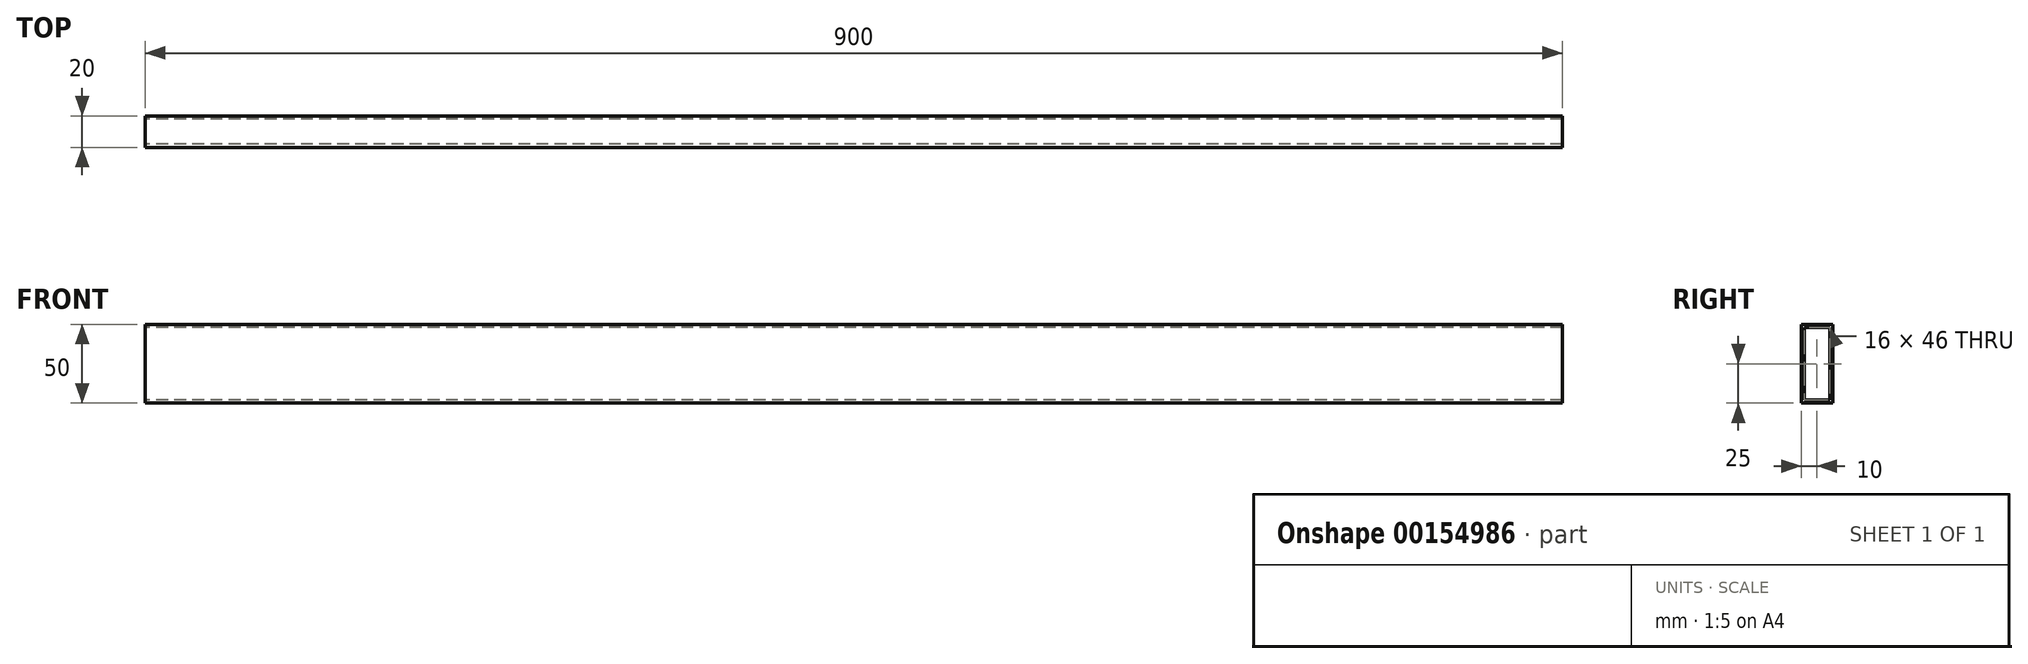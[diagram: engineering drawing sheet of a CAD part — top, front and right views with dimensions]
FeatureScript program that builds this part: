
annotation { "Feature Type Name" : "Feature", "Feature Type Description" : "" }
export const myFeature = defineFeature(function(context is Context, id is Id, definition is map)
    precondition{}
    {
        {
            var Q0;
            Q0=qCreatedBy(makeId("Right.planeOp"),FACE);
            var sketch = newSketch(context, id + "F0", { "sketchPlane" : qUnion([Q0])});
            skLineSegment(sketch, "E0.bottom", {"start": v(-10, 25) * mm, "end": v(10, 25) * mm});
            skLineSegment(sketch, "E0.top", {"start": v(-10, -25) * mm, "end": v(10, -25) * mm});
            skLineSegment(sketch, "E0.left", {"start": v(-10, 25) * mm, "end": v(-10, -25) * mm});
            skLineSegment(sketch, "E0.right", {"start": v(10, 25) * mm, "end": v(10, -25) * mm});
            skSolve(sketch);
        }
        {
            var Q0;
            Q0=makeQuery(id+"F0.imprint","IMPRINT",FACE,{"disambiguationData":[TD([[makeQuery(id+"F0.imprint","IMPRINT",EDGE,{"derivedFrom":sQuery(id+"F0.wireOp",EDGE,"E0.bottom")}),-1.0]])]});
            extrude(context, id + "F1", {"entities" : qUnion([Q0]), "endBound" : BoundingType.SYMMETRIC, "depth" : 900 * mm});
        }
        {
            var Q0;
            Q0=makeQuery(id+"F1.opExtrude","CAP_FACE",FACE,{"disambiguationData":[OSD([sQuery(id+"F0.wireOp",EDGE,"E0.bottom"),sQuery(id+"F0.wireOp",EDGE,"E0.top"),sQuery(id+"F0.wireOp",EDGE,"E0.left"),sQuery(id+"F0.wireOp",EDGE,"E0.right")])],"isStart":true});
            var sketch = newSketch(context, id + "F2", { "sketchPlane" : qUnion([Q0])});
            skLineSegment(sketch, "E1.bottom", {"start": v(8, 23) * mm, "end": v(-8, 23) * mm});
            skLineSegment(sketch, "E1.top", {"start": v(8, -23) * mm, "end": v(-8, -23) * mm});
            skLineSegment(sketch, "E1.left", {"start": v(8, 23) * mm, "end": v(8, -23) * mm});
            skLineSegment(sketch, "E1.right", {"start": v(-8, 23) * mm, "end": v(-8, -23) * mm});
            skPoint(sketch, "E1.middle", {"position": v(0, 0) * mm});
            skSolve(sketch);
        }
        {
            var Q0;
            Q0=makeQuery(id+"F2.imprint","IMPRINT",FACE,{"disambiguationData":[TD([[makeQuery(id+"F2.imprint","IMPRINT",EDGE,{"derivedFrom":sQuery(id+"F2.wireOp",EDGE,"E1.bottom")}),1.0]])]});
            extrude(context, id + "F3", {"entities" : qUnion([Q0]), "operationType" : NewBodyOperationType.REMOVE, "endBound" : BoundingType.THROUGH_ALL, "oppositeDirection" : true, "depth" : 25 * mm});
        }
        {
            var Q0;
            Q0=makeQuery(id+"F1.opExtrude","SWEPT_FACE",FACE,{"disambiguationData":[OSD([sQuery(id+"F0.wireOp",EDGE,"E0.bottom")])]});
            var sketch = newSketch(context, id + "F4", { "sketchPlane" : qUnion([Q0])});
            skPoint(sketch, "E2", {"position": v(-374.9, 0) * mm});
            skPoint(sketch, "E3.MirrorP", {"position": v(374.9, 0) * mm});
            skSolve(sketch);
        }
        {
            var Q0;
            Q0=makeQuery(id+"F1.opExtrude","CAP_FACE",FACE,{"disambiguationData":[OSD([sQuery(id+"F0.wireOp",EDGE,"E0.bottom"),sQuery(id+"F0.wireOp",EDGE,"E0.top"),sQuery(id+"F0.wireOp",EDGE,"E0.left"),sQuery(id+"F0.wireOp",EDGE,"E0.right")])],"isStart":false});
            var sketch = newSketch(context, id + "F5", { "sketchPlane" : qUnion([Q0])});
            skPoint(sketch, "E4", {"position": v(0, 17) * mm});
            skSolve(sketch);
        }
        {
            var Q0;
            Q0=makeQuery(id+"F1.opExtrude","CAP_FACE",FACE,{"disambiguationData":[OSD([sQuery(id+"F0.wireOp",EDGE,"E0.bottom"),sQuery(id+"F0.wireOp",EDGE,"E0.top"),sQuery(id+"F0.wireOp",EDGE,"E0.left"),sQuery(id+"F0.wireOp",EDGE,"E0.right")])],"isStart":true});
            var sketch = newSketch(context, id + "F6", { "sketchPlane" : qUnion([Q0])});
            skPoint(sketch, "E5", {"position": v(0, 17) * mm});
            skSolve(sketch);
        }
    });
